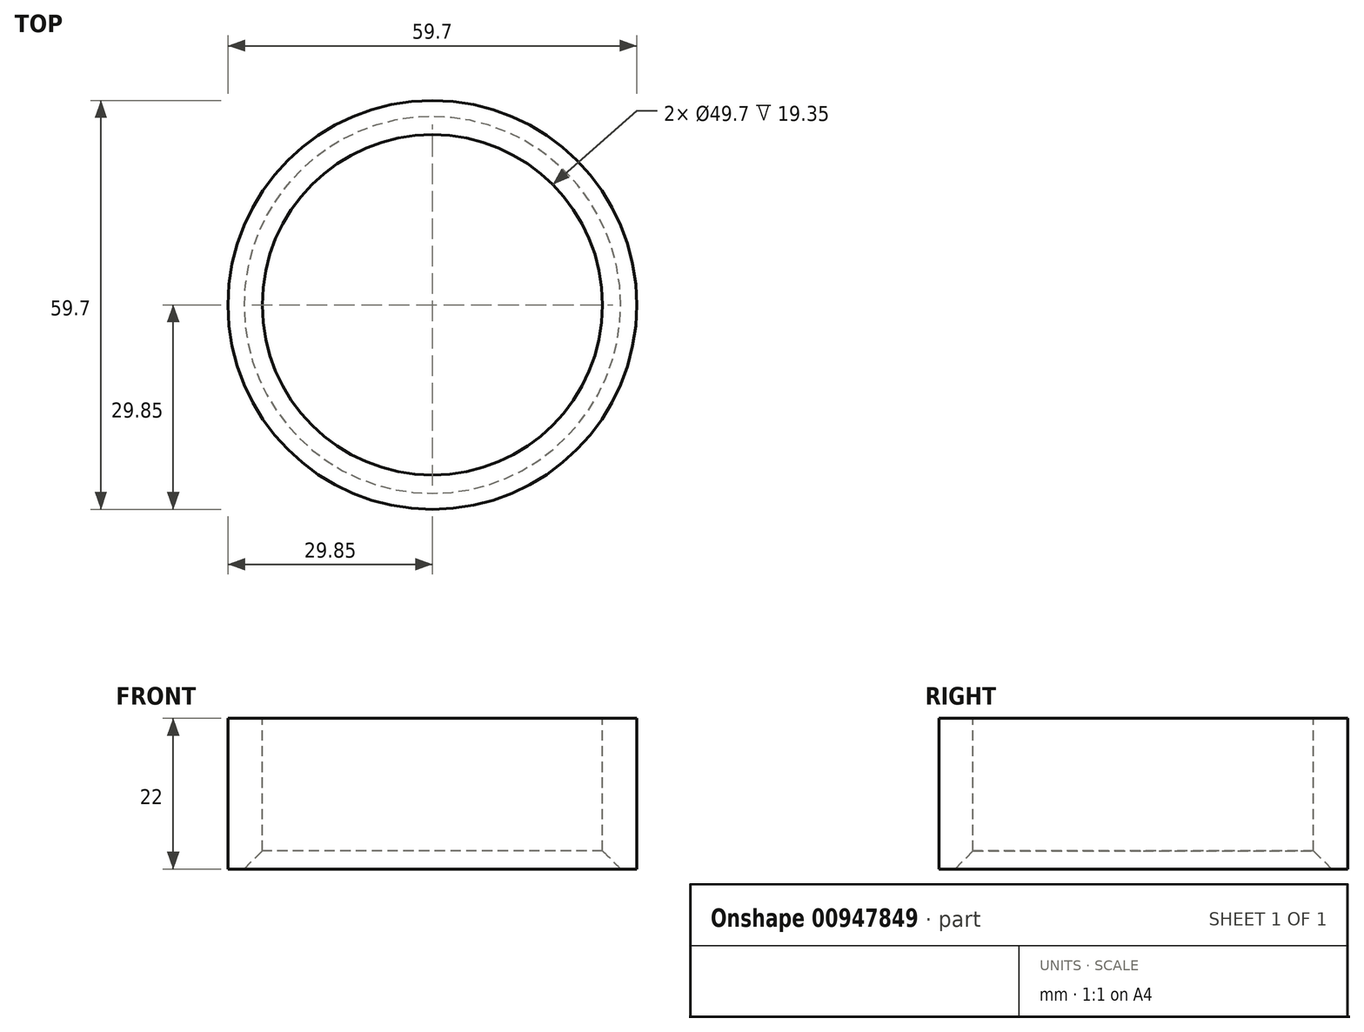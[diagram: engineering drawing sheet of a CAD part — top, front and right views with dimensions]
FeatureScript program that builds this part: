
annotation { "Feature Type Name" : "Feature", "Feature Type Description" : "" }
export const myFeature = defineFeature(function(context is Context, id is Id, definition is map)
    precondition{}
    {
        {
            var Q0;
            Q0=qCreatedBy(makeId("Front.planeOp"),FACE);
            var sketch = newSketch(context, id + "F0", { "sketchPlane" : qUnion([Q0])});
            skLineSegment(sketch, "E0", {"start": v(24.85, 0) * mm, "end": v(24.85, -19.35) * mm});
            skLineSegment(sketch, "E1", {"start": v(24.85, -19.35) * mm, "end": v(27.5, -22) * mm});
            skLineSegment(sketch, "E2", {"start": v(27.5, -22) * mm, "end": v(29.85, -22) * mm});
            skLineSegment(sketch, "E3", {"start": v(29.85, -22) * mm, "end": v(29.85, 0) * mm});
            skLineSegment(sketch, "E4", {"start": v(29.85, 0) * mm, "end": v(24.85, 0) * mm});
            skLineSegment(sketch, "E5", {"start": v(0, 0) * mm, "end": v(0, -10.6) * mm, "construction": true});
            skSolve(sketch);
        }
        {
            var Q0;
            Q0=makeQuery(id+"F0.imprint","IMPRINT",FACE,{"disambiguationData":[TD([[makeQuery(id+"F0.imprint","IMPRINT",EDGE,{"derivedFrom":sQuery(id+"F0.wireOp",EDGE,"E0")}),1.0]])]});
            var Q1;
            Q1=sQuery(id+"F0.wireOp",EDGE,"E5");
            revolve(context, id + "F1", {"surfaceOperationType" : NewSurfaceOperationType.NEW, "entities" : qUnion([Q0]), "axis" : qUnion([Q1]), "revolveType" : RevolveType.FULL});
        }
    });
